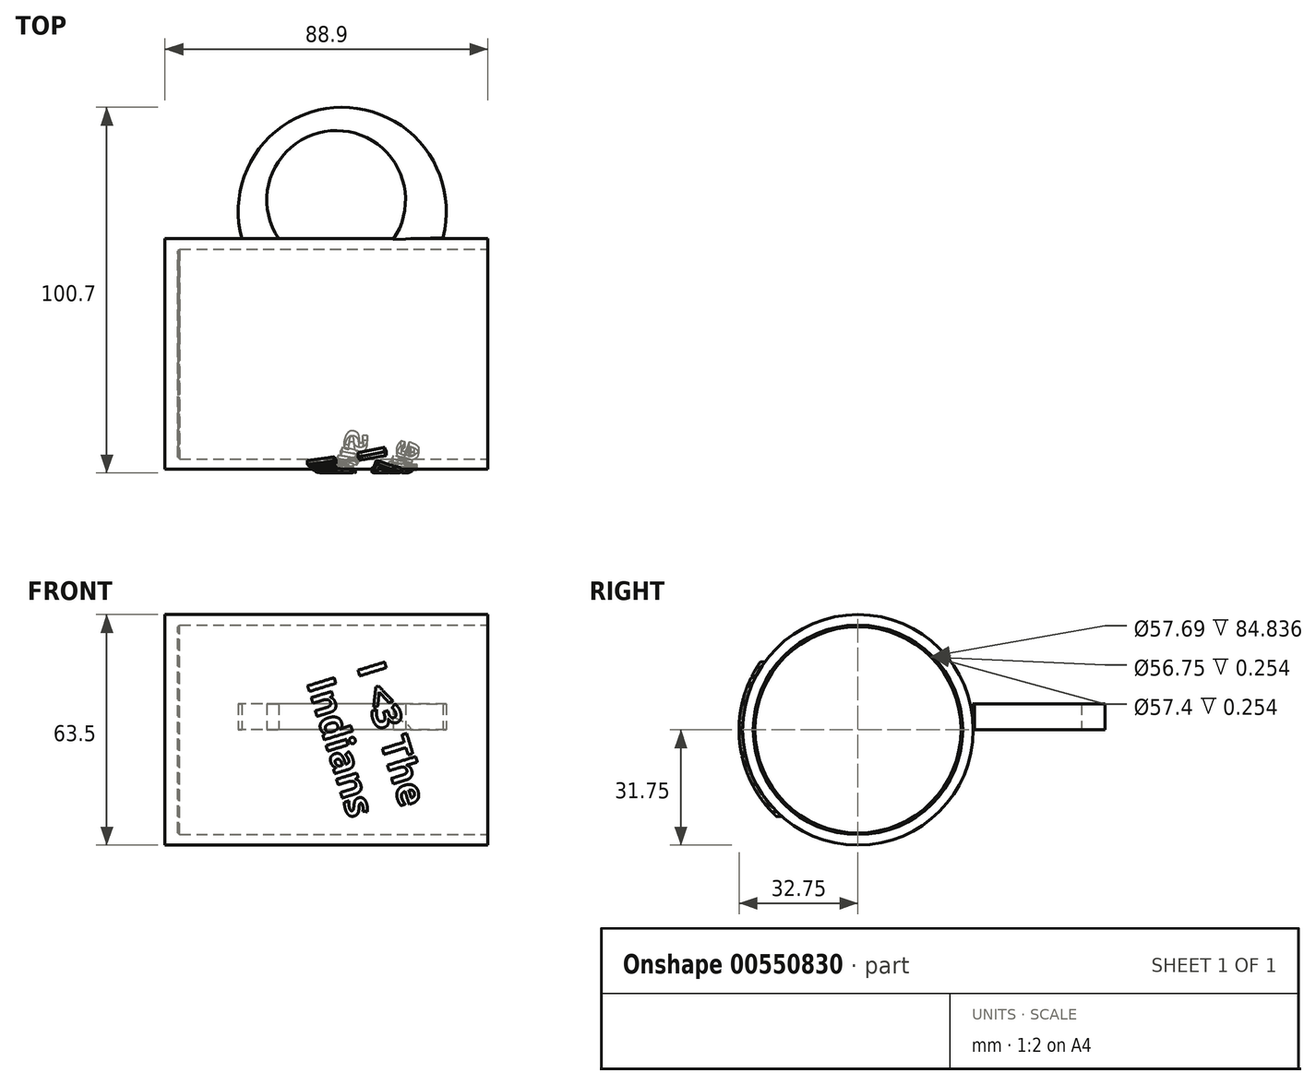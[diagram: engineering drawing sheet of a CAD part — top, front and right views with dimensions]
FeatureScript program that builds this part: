
annotation { "Feature Type Name" : "Feature", "Feature Type Description" : "" }
export const myFeature = defineFeature(function(context is Context, id is Id, definition is map)
    precondition{}
    {
        {
            var Q0;
            Q0=qCreatedBy(makeId("Right.planeOp"),FACE);
            var sketch = newSketch(context, id + "F0", { "sketchPlane" : qUnion([Q0])});
            skCircle(sketch, "E0", {"center": v(0, 0) * mm, "radius": 31.75 * mm});
            skSolve(sketch);
        }
        {
            var Q0;
            Q0 = qSketchRegion(id + "F0", true);
            extrude(context, id + "F1", {"entities" : qUnion([Q0]), "oppositeDirection" : true, "depth" : 88.9 * mm, "offsetDistance" : 25.4 * mm});
        }
        {
            var Q0;
            Q0=qCreatedBy(makeId("Right.planeOp"),FACE);
            var sketch = newSketch(context, id + "F2", { "sketchPlane" : qUnion([Q0])});
            skCircle(sketch, "E1", {"center": v(0, 0) * mm, "radius": 28.7 * mm});
            skSolve(sketch);
        }
        {
            var Q0;
            Q0 = qSketchRegion(id + "F2", true);
            extrude(context, id + "F3", {"entities" : qUnion([Q0]), "operationType" : NewBodyOperationType.REMOVE, "oppositeDirection" : true, "depth" : 85.1 * mm, "offsetDistance" : 25.4 * mm});
        }
        {
            var Q0;
            Q0=qCreatedBy(makeId("Top.planeOp"),FACE);
            var sketch = newSketch(context, id + "F4", { "sketchPlane" : qUnion([Q0])});
            skArc(sketch, "E2", {"start": v(-12.37, 32.1) * mm, "mid": v(-40.28, 67.95) * mm, "end": v(-67.73, 31.75) * mm});
            skArc(sketch, "E3", {"start": v(-26.1, 31.56) * mm, "mid": v(-41.6, 61.54) * mm, "end": v(-57.62, 31.83) * mm});
            skLineSegment(sketch, "E4", {"start": v(-26.1, 31.56) * mm, "end": v(-12.37, 32.1) * mm});
            skLineSegment(sketch, "E5", {"start": v(-57.62, 31.83) * mm, "end": v(-67.73, 31.75) * mm});
            skSolve(sketch);
        }
        {
            var Q0;
            Q0 = qSketchRegion(id + "F4", true);
            extrude(context, id + "F5", {"entities" : qUnion([Q0]), "operationType" : NewBodyOperationType.ADD, "depth" : 7.11 * mm, "offsetDistance" : 25.4 * mm});
        }
        {
            var Q0;
            Q0=qCreatedBy(makeId("Front.planeOp"),FACE);
            var sketch = newSketch(context, id + "F6", { "sketchPlane" : qUnion([Q0])});
            skText(sketch, "E6", { "text": "I <3 The \nIndians", "fontName": "OpenSans-Bold.ttf"});
            const initialGuessF6  = {"E6": [-0.03603, 0.01734, 0.29544, -0.95536, 0.0077]};
            skSetInitialGuess(sketch, initialGuessF6);
            skSolve(sketch);
        }
        {
            var Q0;
            Q0 = qSketchRegion(id + "F6", true);
            extrude(context, id + "F7", {"entities" : qUnion([Q0]), "operationType" : NewBodyOperationType.ADD, "depth" : 34.04 * mm, "offsetDistance" : 25.4 * mm});
        }
        {
            var Q0;
            Q0=qCreatedBy(makeId("Right.planeOp"),FACE);
            var sketch = newSketch(context, id + "F8", { "sketchPlane" : qUnion([Q0])});
            skCircle(sketch, "E7", {"center": v(0, 0) * mm, "radius": 28.37 * mm});
            skSolve(sketch);
        }
        {
            var Q0;
            Q0 = qSketchRegion(id + "F8", true);
            extrude(context, id + "F9", {"entities" : qUnion([Q0]), "operationType" : NewBodyOperationType.REMOVE, "oppositeDirection" : true, "depth" : 85.34 * mm, "offsetDistance" : 25.4 * mm});
        }
        {
            var Q0;
            Q0=qCreatedBy(makeId("Right.planeOp"),FACE);
            var sketch = newSketch(context, id + "F10", { "sketchPlane" : qUnion([Q0])});
            skArc(sketch, "E8", {"start": v(29.19, 14.86) * mm, "mid": v(-32.74, -0.83) * mm, "end": v(29.9, -13.37) * mm});
            skLineSegment(sketch, "E9", {"start": v(29.9, -13.37) * mm, "end": v(35.73, -19.5) * mm});
            skLineSegment(sketch, "E10", {"start": v(29.19, 14.86) * mm, "end": v(35.03, 20.72) * mm});
            skArc(sketch, "E11", {"start": v(35.03, 20.72) * mm, "mid": v(-45.83, -0.8) * mm, "end": v(35.73, -19.5) * mm});
            skSolve(sketch);
        }
        {
            var Q0;
            Q0 = qSketchRegion(id + "F10", true);
            extrude(context, id + "F11", {"entities" : qUnion([Q0]), "operationType" : NewBodyOperationType.REMOVE, "oppositeDirection" : true, "depth" : 64 * mm, "offsetDistance" : 25.4 * mm});
        }
        {
            var Q0;
            Q0=qCreatedBy(makeId("Right.planeOp"),FACE);
            var sketch = newSketch(context, id + "F12", { "sketchPlane" : qUnion([Q0])});
            skCircle(sketch, "E12", {"center": v(0, 0) * mm, "radius": 28.84 * mm});
            skSolve(sketch);
        }
        {
            var Q0;
            Q0=makeQuery(id+"F12.imprint","IMPRINT",FACE,{"disambiguationData":[TD([[makeQuery(id+"F12.imprint","IMPRINT",EDGE,{"derivedFrom":sQuery(id+"F12.wireOp",EDGE,"E12")}),1.0]])]});
            extrude(context, id + "F13", {"entities" : qUnion([Q0]), "operationType" : NewBodyOperationType.REMOVE, "oppositeDirection" : true, "depth" : 84.84 * mm, "offsetDistance" : 25.4 * mm});
        }
    });
